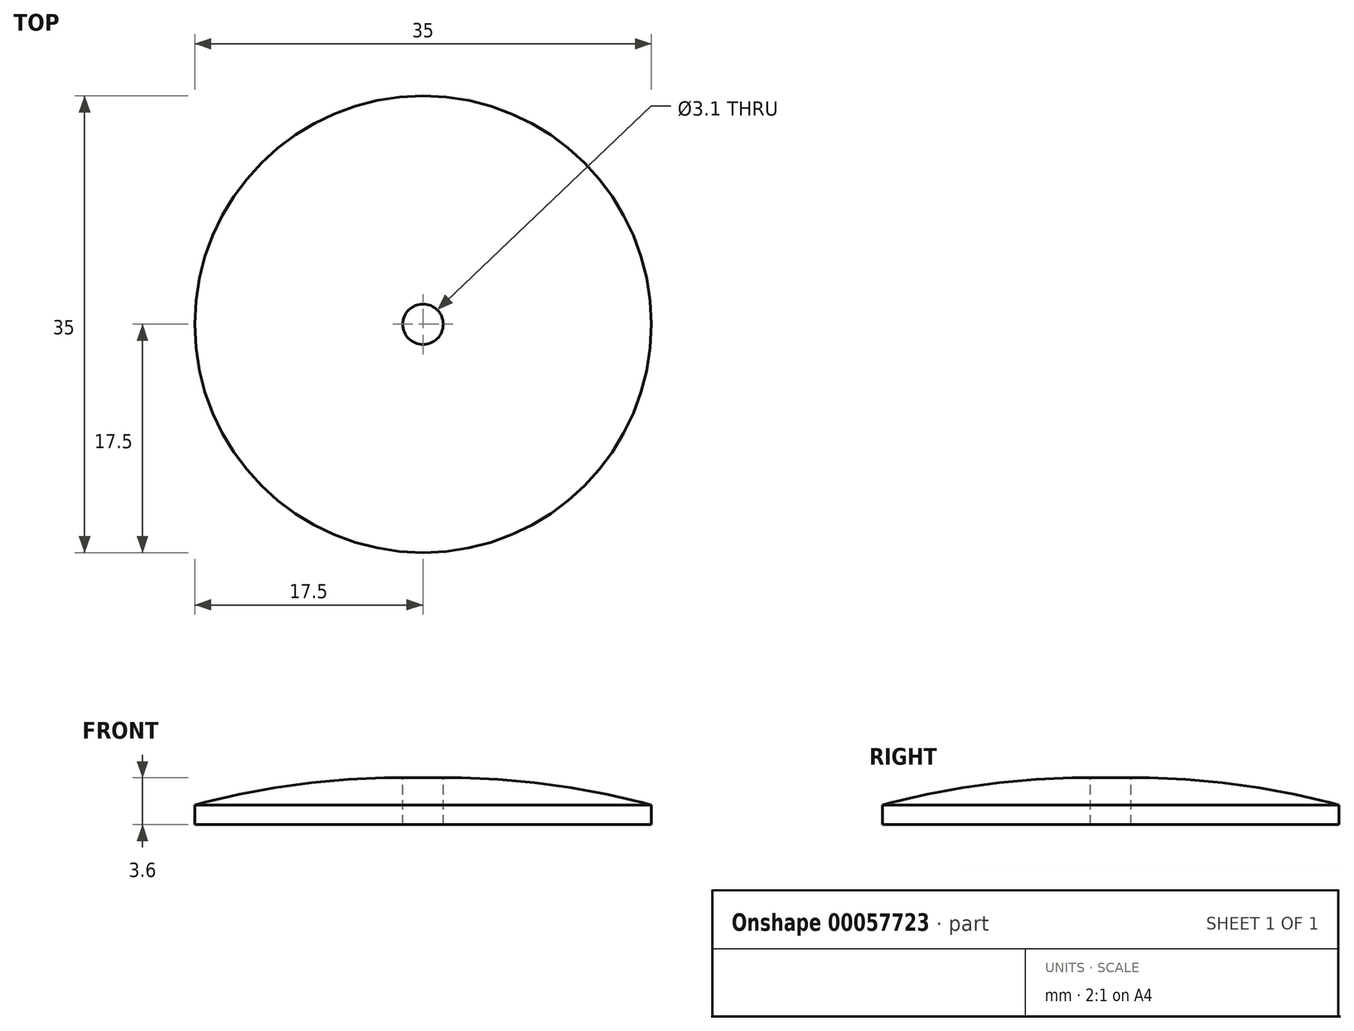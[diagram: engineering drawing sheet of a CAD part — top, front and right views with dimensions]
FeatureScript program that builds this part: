
annotation { "Feature Type Name" : "Feature", "Feature Type Description" : "" }
export const myFeature = defineFeature(function(context is Context, id is Id, definition is map)
    precondition{}
    {
        {
            var Q0;
            Q0=qCreatedBy(makeId("Front.planeOp"),FACE);
            var sketch = newSketch(context, id + "F0", { "sketchPlane" : qUnion([Q0])});
            skLineSegment(sketch, "E0.bottom", {"start": v(0, 3.6) * mm, "end": v(-1.55, 3.6) * mm});
            skLineSegment(sketch, "E0.top", {"start": v(0, 0) * mm, "end": v(-1.55, 0) * mm});
            skLineSegment(sketch, "E0.left", {"start": v(0, 3.6) * mm, "end": v(0, 0) * mm});
            skLineSegment(sketch, "E0.right", {"start": v(-1.55, 3.6) * mm, "end": v(-1.55, 0) * mm});
            skArc(sketch, "E1", {"start": v(-1.55, 3.6) * mm, "mid": v(-9.6, 3.07) * mm, "end": v(-17.5, 1.5) * mm});
            skLineSegment(sketch, "E2", {"start": v(-17.5, 1.5) * mm, "end": v(-17.5, 0) * mm});
            skLineSegment(sketch, "E3", {"start": v(-17.5, 0) * mm, "end": v(0, 0) * mm});
            skSolve(sketch);
        }
        {
            var Q0;
            {var subQ0=sQuery(id+"F0.wireOp",EDGE,"E0.right");Q0=makeQuery(id+"F0.imprint","IMPRINT",FACE,{"disambiguationData":[TD([[makeQuery(id+"F0.imprint","IMPRINT",EDGE,{"derivedFrom":subQ0}),-1.0]])]});}
            var Q1;
            Q1=sQuery(id+"F0.wireOp",EDGE,"E0.left");
            revolve(context, id + "F1", {"entities" : qUnion([Q0]), "axis" : qUnion([Q1]), "revolveType" : RevolveType.FULL});
        }
    });
